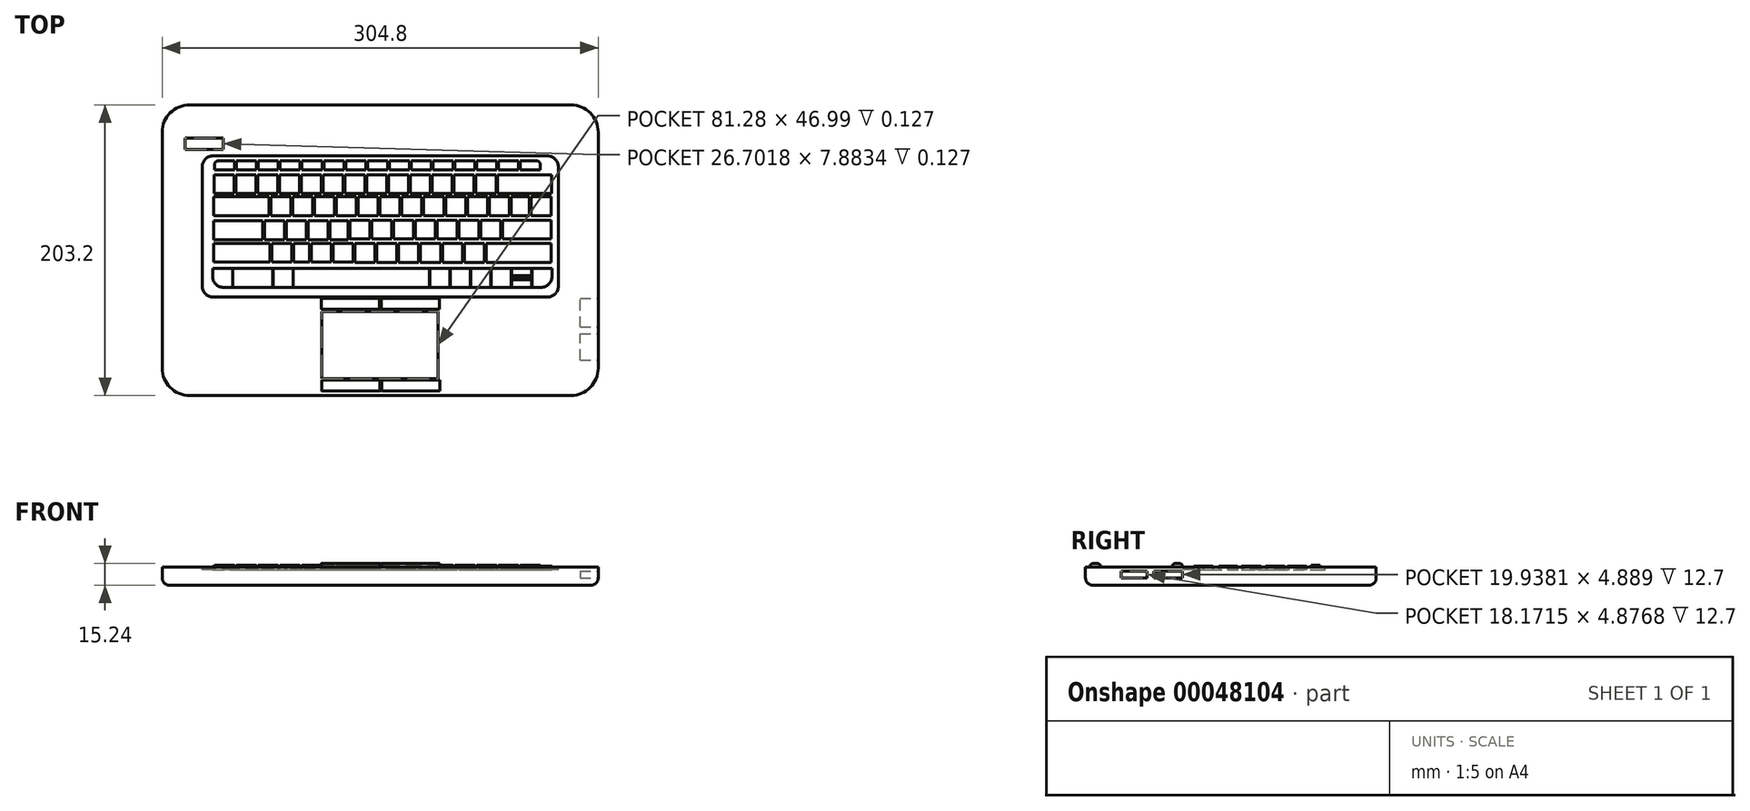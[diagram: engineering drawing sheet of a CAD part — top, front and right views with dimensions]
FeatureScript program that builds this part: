
annotation { "Feature Type Name" : "Feature", "Feature Type Description" : "" }
export const myFeature = defineFeature(function(context is Context, id is Id, definition is map)
    precondition{}
    {
        {
            var Q0;
            Q0=qCreatedBy(makeId("Top.planeOp"),FACE);
            var sketch = newSketch(context, id + "F0", { "sketchPlane" : qUnion([Q0])});
            skLineSegment(sketch, "E0.bottom", {"start": v(-133.35, 101.6) * mm, "end": v(133.35, 101.6) * mm});
            skLineSegment(sketch, "E0.top", {"start": v(-133.35, -101.6) * mm, "end": v(133.35, -101.6) * mm});
            skLineSegment(sketch, "E0.left", {"start": v(-152.4, 82.55) * mm, "end": v(-152.4, -82.55) * mm});
            skLineSegment(sketch, "E0.right", {"start": v(152.4, 82.55) * mm, "end": v(152.4, -82.55) * mm});
            skPoint(sketch, "E1.visualSharp", {"position": v(-152.4, 101.6) * mm});
            skArc(sketch, "E1.filletArc", {"start": v(-133.35, 101.6) * mm, "mid": v(-146.82, 96.02) * mm, "end": v(-152.4, 82.55) * mm});
            skPoint(sketch, "E2.visualSharp", {"position": v(152.4, 101.6) * mm});
            skArc(sketch, "E2.filletArc", {"start": v(152.4, 82.55) * mm, "mid": v(146.82, 96.02) * mm, "end": v(133.35, 101.6) * mm});
            skPoint(sketch, "E3.visualSharp", {"position": v(152.4, -101.6) * mm});
            skArc(sketch, "E3.filletArc", {"start": v(133.35, -101.6) * mm, "mid": v(146.82, -96.02) * mm, "end": v(152.4, -82.55) * mm});
            skPoint(sketch, "E4.visualSharp", {"position": v(-152.4, -101.6) * mm});
            skArc(sketch, "E4.filletArc", {"start": v(-152.4, -82.55) * mm, "mid": v(-146.82, -96.02) * mm, "end": v(-133.35, -101.6) * mm});
            skSolve(sketch);
        }
        {
            var Q0;
            Q0=makeQuery(id+"F0.imprint","IMPRINT",FACE,{"disambiguationData":[TD([[makeQuery(id+"F0.imprint","IMPRINT",EDGE,{"derivedFrom":sQuery(id+"F0.wireOp",EDGE,"E0.bottom")}),-1.0]])]});
            extrude(context, id + "F1", {"entities" : qUnion([Q0]), "depth" : 12.7 * mm});
        }
        {
            var Q0;
            Q0=makeQuery(id+"F1.opExtrude","CAP_EDGE",EDGE,{"disambiguationData":[OSD([sQuery(id+"F0.wireOp",EDGE,"E0.top")])],"isStart":true});
            fillet(context, id + "F2", {"entities" : qUnion([Q0]), "radius" : 5.08 * mm, "tangentPropagation" : true, "allowEdgeOverflow" : false});
        }
        {
            var Q0;
            Q0=makeQuery(id+"F1.opExtrude","CAP_FACE",FACE,{"disambiguationData":[OSD([sQuery(id+"F0.wireOp",EDGE,"E0.bottom"),sQuery(id+"F0.wireOp",EDGE,"E0.top"),sQuery(id+"F0.wireOp",EDGE,"E0.left"),sQuery(id+"F0.wireOp",EDGE,"E0.right"),sQuery(id+"F0.wireOp",EDGE,"E1.filletArc"),sQuery(id+"F0.wireOp",EDGE,"E2.filletArc"),sQuery(id+"F0.wireOp",EDGE,"E3.filletArc"),sQuery(id+"F0.wireOp",EDGE,"E4.filletArc")])],"isStart":false});
            var sketch = newSketch(context, id + "F3", { "sketchPlane" : qUnion([Q0])});
            skLineSegment(sketch, "E5.bottom", {"start": v(-116.84, -32.8) * mm, "end": v(116.84, -32.8) * mm});
            skLineSegment(sketch, "E5.top", {"start": v(-116.84, 65.93) * mm, "end": v(116.84, 65.93) * mm});
            skLineSegment(sketch, "E5.left", {"start": v(-124.46, -25.18) * mm, "end": v(-124.46, 58.31) * mm});
            skLineSegment(sketch, "E5.right", {"start": v(124.46, -25.18) * mm, "end": v(124.46, 58.31) * mm});
            skPoint(sketch, "E6.visualSharp", {"position": v(-124.46, 65.93) * mm});
            skArc(sketch, "E6.filletArc", {"start": v(-116.84, 65.93) * mm, "mid": v(-122.23, 63.7) * mm, "end": v(-124.46, 58.31) * mm});
            skPoint(sketch, "E7.visualSharp", {"position": v(124.46, 65.93) * mm});
            skArc(sketch, "E7.filletArc", {"start": v(124.46, 58.31) * mm, "mid": v(122.23, 63.7) * mm, "end": v(116.84, 65.93) * mm});
            skPoint(sketch, "E8.visualSharp", {"position": v(124.46, -32.8) * mm});
            skArc(sketch, "E8.filletArc", {"start": v(116.84, -32.8) * mm, "mid": v(122.23, -30.57) * mm, "end": v(124.46, -25.18) * mm});
            skPoint(sketch, "E9.visualSharp", {"position": v(-124.46, -32.8) * mm});
            skArc(sketch, "E9.filletArc", {"start": v(-124.46, -25.18) * mm, "mid": v(-122.23, -30.57) * mm, "end": v(-116.84, -32.8) * mm});
            skSolve(sketch);
        }
        {
            var Q0;
            Q0 = qSketchRegion(id + "F3", true);
            extrude(context, id + "F4", {"entities" : qUnion([Q0]), "operationType" : NewBodyOperationType.REMOVE, "oppositeDirection" : true, "depth" : 1.78 * mm});
        }
        {
            var Q0;
            Q0=makeQuery(id+"F4.boolean.opBoolean","COPY",FACE,{"derivedFrom":makeQuery(id+"F4.opExtrude","CAP_FACE",FACE,{"disambiguationData":[OSD([sQuery(id+"F3.wireOp",EDGE,"E5.bottom"),sQuery(id+"F3.wireOp",EDGE,"E5.top"),sQuery(id+"F3.wireOp",EDGE,"E5.left"),sQuery(id+"F3.wireOp",EDGE,"E5.right"),sQuery(id+"F3.wireOp",EDGE,"E6.filletArc"),sQuery(id+"F3.wireOp",EDGE,"E7.filletArc"),sQuery(id+"F3.wireOp",EDGE,"E8.filletArc"),sQuery(id+"F3.wireOp",EDGE,"E9.filletArc")])],"isStart":false})});
            var sketch = newSketch(context, id + "F5", { "sketchPlane" : qUnion([Q0])});
            skLineSegment(sketch, "E10.bottom", {"start": v(-60.72, -12.77) * mm, "end": v(34.53, -12.77) * mm});
            skLineSegment(sketch, "E10.top", {"start": v(-60.72, -25.99) * mm, "end": v(34.53, -25.99) * mm});
            skLineSegment(sketch, "E10.left", {"start": v(-60.72, -12.77) * mm, "end": v(-60.72, -25.99) * mm});
            skLineSegment(sketch, "E10.right", {"start": v(34.53, -12.77) * mm, "end": v(34.53, -25.99) * mm});
            skLineSegment(sketch, "E11.top", {"start": v(97.18, -32.93) * mm, "end": v(110.41, -32.93) * mm});
            skPoint(sketch, "E12.visualSharp", {"position": v(124.4, -32.93) * mm});
            skLineSegment(sketch, "E13.bottom", {"start": v(-60.97, -25.99) * mm, "end": v(-74.97, -25.99) * mm});
            skLineSegment(sketch, "E13.top", {"start": v(-60.97, -12.76) * mm, "end": v(-74.97, -12.76) * mm});
            skLineSegment(sketch, "E13.left", {"start": v(-60.97, -25.99) * mm, "end": v(-60.97, -12.76) * mm});
            skLineSegment(sketch, "E13.right", {"start": v(-74.97, -25.99) * mm, "end": v(-74.97, -12.76) * mm});
            skLineSegment(sketch, "E14.bottom", {"start": v(34.78, -12.76) * mm, "end": v(48.78, -12.76) * mm});
            skLineSegment(sketch, "E14.top", {"start": v(34.78, -25.99) * mm, "end": v(48.78, -25.99) * mm});
            skLineSegment(sketch, "E14.left", {"start": v(34.78, -12.76) * mm, "end": v(34.78, -25.99) * mm});
            skLineSegment(sketch, "E14.right", {"start": v(48.78, -12.76) * mm, "end": v(48.78, -25.99) * mm});
            skLineSegment(sketch, "E15.bottom", {"start": v(49.03, -12.76) * mm, "end": v(63.03, -12.76) * mm});
            skLineSegment(sketch, "E15.top", {"start": v(49.03, -25.99) * mm, "end": v(63.03, -25.99) * mm});
            skLineSegment(sketch, "E15.left", {"start": v(49.03, -12.76) * mm, "end": v(49.03, -25.99) * mm});
            skLineSegment(sketch, "E15.right", {"start": v(63.03, -12.76) * mm, "end": v(63.03, -25.99) * mm});
            skLineSegment(sketch, "E16.bottom", {"start": v(63.28, -12.76) * mm, "end": v(77.28, -12.76) * mm});
            skLineSegment(sketch, "E16.top", {"start": v(63.28, -25.99) * mm, "end": v(77.28, -25.99) * mm});
            skLineSegment(sketch, "E16.left", {"start": v(63.28, -12.76) * mm, "end": v(63.28, -25.99) * mm});
            skLineSegment(sketch, "E16.right", {"start": v(77.28, -12.76) * mm, "end": v(77.28, -25.99) * mm});
            skLineSegment(sketch, "E17", {"start": v(-88.97, -25.99) * mm, "end": v(-102.96, -25.99) * mm});
            skLineSegment(sketch, "E18", {"start": v(-102.96, -12.76) * mm, "end": v(-88.97, -12.76) * mm});
            skLineSegment(sketch, "E19.bottom", {"start": v(-117.21, -12.76) * mm, "end": v(-103.21, -12.76) * mm});
            skLineSegment(sketch, "E19.top", {"start": v(-109.6, -25.99) * mm, "end": v(-103.21, -25.99) * mm});
            skLineSegment(sketch, "E19.left", {"start": v(-117.21, -12.76) * mm, "end": v(-117.21, -18.37) * mm});
            skLineSegment(sketch, "E19.right", {"start": v(-103.21, -12.76) * mm, "end": v(-103.21, -25.99) * mm});
            skPoint(sketch, "E20.visualSharp", {"position": v(-117.21, -25.99) * mm});
            skArc(sketch, "E20.filletArc", {"start": v(-117.21, -18.37) * mm, "mid": v(-114.98, -23.76) * mm, "end": v(-109.6, -25.99) * mm});
            skLineSegment(sketch, "E21", {"start": v(-102.96, -12.76) * mm, "end": v(-102.96, -25.99) * mm});
            skLineSegment(sketch, "E22", {"start": v(-88.97, -12.76) * mm, "end": v(-102.96, -12.76) * mm});
            skLineSegment(sketch, "E23.bottom", {"start": v(77.53, -12.76) * mm, "end": v(91.53, -12.76) * mm});
            skLineSegment(sketch, "E23.top", {"start": v(77.53, -25.99) * mm, "end": v(91.53, -25.99) * mm});
            skLineSegment(sketch, "E23.left", {"start": v(77.53, -12.76) * mm, "end": v(77.53, -25.99) * mm});
            skLineSegment(sketch, "E23.right", {"start": v(91.53, -12.76) * mm, "end": v(91.53, -25.99) * mm});
            skPoint(sketch, "E24.visualSharp", {"position": v(129.05, -2.73) * mm});
            skLineSegment(sketch, "E25.top", {"start": v(91.78, -25.99) * mm, "end": v(105.78, -25.99) * mm});
            skLineSegment(sketch, "E25.left", {"start": v(91.78, -19.37) * mm, "end": v(91.78, -25.99) * mm});
            skLineSegment(sketch, "E25.right", {"start": v(105.78, -19.37) * mm, "end": v(105.78, -25.99) * mm});
            skLineSegment(sketch, "E26.top", {"start": v(248.95, -19.37) * mm, "end": v(262.95, -19.37) * mm});
            skLineSegment(sketch, "E27", {"start": v(-88.97, -12.76) * mm, "end": v(-88.97, -25.99) * mm});
            skLineSegment(sketch, "E28.bottom", {"start": v(-89.22, -12.76) * mm, "end": v(-75.22, -12.76) * mm});
            skLineSegment(sketch, "E28.top", {"start": v(-89.22, -25.99) * mm, "end": v(-75.22, -25.99) * mm});
            skLineSegment(sketch, "E28.left", {"start": v(-89.22, -12.76) * mm, "end": v(-89.22, -25.99) * mm});
            skLineSegment(sketch, "E28.right", {"start": v(-75.22, -12.76) * mm, "end": v(-75.22, -25.99) * mm});
            skLineSegment(sketch, "E29.bottom", {"start": v(106.03, -12.76) * mm, "end": v(120.03, -12.76) * mm});
            skLineSegment(sketch, "E29.top", {"start": v(106.03, -25.99) * mm, "end": v(112.4, -25.99) * mm});
            skLineSegment(sketch, "E29.left", {"start": v(106.03, -12.76) * mm, "end": v(106.03, -25.99) * mm});
            skLineSegment(sketch, "E29.right", {"start": v(120.03, -12.76) * mm, "end": v(120.03, -18.37) * mm});
            skArc(sketch, "E30.filletArc", {"start": v(112.4, -25.99) * mm, "mid": v(117.8, -23.76) * mm, "end": v(120.03, -18.37) * mm});
            skLineSegment(sketch, "E31.left", {"start": v(91.27, -12.5) * mm, "end": v(91.27, -19.12) * mm});
            skLineSegment(sketch, "E31.right", {"start": v(105.78, -12.5) * mm, "end": v(105.78, -19.12) * mm});
            skLineSegment(sketch, "E32", {"start": v(91.78, -19.37) * mm, "end": v(105.78, -19.37) * mm});
            skLineSegment(sketch, "E33.bottom", {"start": v(91.78, -12.63) * mm, "end": v(105.78, -12.63) * mm});
            skLineSegment(sketch, "E33.top", {"start": v(91.78, -19.25) * mm, "end": v(105.78, -19.25) * mm});
            skLineSegment(sketch, "E33.left", {"start": v(91.78, -12.63) * mm, "end": v(91.78, -19.25) * mm});
            skLineSegment(sketch, "E33.right", {"start": v(105.78, -12.63) * mm, "end": v(105.78, -19.25) * mm});
            skSolve(sketch);
        }
        {
            var Q0;
            Q0=makeQuery(id+"F5.imprint","IMPRINT",FACE,{"disambiguationData":[TD([[makeQuery(id+"F5.imprint","IMPRINT",EDGE,{"derivedFrom":sQuery(id+"F5.wireOp",EDGE,"E19.bottom")}),-1.0]])]});
            var Q1;
            Q1=makeQuery(id+"F5.imprint","IMPRINT",FACE,{"disambiguationData":[TD([[makeQuery(id+"F5.imprint","IMPRINT",EDGE,{"derivedFrom":sQuery(id+"F5.wireOp",EDGE,"E17")}),-1.0]])]});
            var Q2;
            {var subQ2=sQuery(id+"F5.wireOp",EDGE,"E27");Q2=makeQuery(id+"F5.imprint","IMPRINT",FACE,{"disambiguationData":[TD([[makeQuery(id+"F5.imprint","IMPRINT",EDGE,{"derivedFrom":subQ2}),1.0]])]});}
            var Q3;
            Q3=makeQuery(id+"F5.imprint","IMPRINT",FACE,{"disambiguationData":[TD([[makeQuery(id+"F5.imprint","IMPRINT",EDGE,{"derivedFrom":sQuery(id+"F5.wireOp",EDGE,"E13.bottom")}),-1.0]])]});
            var Q4;
            Q4=makeQuery(id+"F5.imprint","IMPRINT",FACE,{"disambiguationData":[TD([[makeQuery(id+"F5.imprint","IMPRINT",EDGE,{"derivedFrom":sQuery(id+"F5.wireOp",EDGE,"E10.bottom")}),-1.0]])]});
            var Q5;
            Q5=makeQuery(id+"F5.imprint","IMPRINT",FACE,{"disambiguationData":[TD([[makeQuery(id+"F5.imprint","IMPRINT",EDGE,{"derivedFrom":sQuery(id+"F5.wireOp",EDGE,"E14.bottom")}),-1.0]])]});
            var Q6;
            Q6=makeQuery(id+"F5.imprint","IMPRINT",FACE,{"disambiguationData":[TD([[makeQuery(id+"F5.imprint","IMPRINT",EDGE,{"derivedFrom":sQuery(id+"F5.wireOp",EDGE,"E15.bottom")}),-1.0]])]});
            var Q7;
            Q7=makeQuery(id+"F5.imprint","IMPRINT",FACE,{"disambiguationData":[TD([[makeQuery(id+"F5.imprint","IMPRINT",EDGE,{"derivedFrom":sQuery(id+"F5.wireOp",EDGE,"E16.bottom")}),-1.0]])]});
            var Q8;
            Q8=makeQuery(id+"F5.imprint","IMPRINT",FACE,{"disambiguationData":[TD([[makeQuery(id+"F5.imprint","IMPRINT",EDGE,{"derivedFrom":sQuery(id+"F5.wireOp",EDGE,"E23.top")}),1.0]])]});
            var Q9;
            Q9=makeQuery(id+"F5.imprint","IMPRINT",FACE,{"disambiguationData":[TD([[makeQuery(id+"F5.imprint","IMPRINT",EDGE,{"derivedFrom":sQuery(id+"F5.wireOp",EDGE,"E29.bottom")}),-1.0]])]});
            var Q10;
            {var subQ0=sQuery(id+"F5.wireOp",EDGE,"E33.bottom");Q10=makeQuery(id+"F5.imprint","IMPRINT",FACE,{"disambiguationData":[TD([[makeQuery(id+"F5.imprint","IMPRINT",EDGE,{"derivedFrom":subQ0}),-1.0]])]});}
            var Q11;
            Q11=makeQuery(id+"F5.imprint","IMPRINT",FACE,{"disambiguationData":[TD([[makeQuery(id+"F5.imprint","IMPRINT",EDGE,{"derivedFrom":sQuery(id+"F5.wireOp",EDGE,"E25.top")}),1.0]])]});
            extrude(context, id + "F6", {"entities" : qUnion([Q0, Q1, Q2, Q3, Q4, Q5, Q6, Q7, Q8, Q9, Q10, Q11]), "operationType" : NewBodyOperationType.ADD, "endBound" : BoundingType.SYMMETRIC, "depth" : 5.08 * mm});
        }
        {
            var Q0;
            Q0=makeQuery(id+"F6.opExtrude","CAP_EDGE",EDGE,{"disambiguationData":[OSD([sQuery(id+"F5.wireOp",EDGE,"E33.top")])],"isStart":false});
            chamfer(context, id + "F7", {"entities" : qUnion([Q0]), "width" : 1.27 * mm, "tangentPropagation" : true});
        }
        {
            var Q0;
            Q0=makeQuery(id+"F6.opExtrude","CAP_EDGE",EDGE,{"disambiguationData":[OSD([sQuery(id+"F5.wireOp",EDGE,"E32")])],"isStart":false});
            chamfer(context, id + "F8", {"entities" : qUnion([Q0]), "width" : 1.27 * mm, "tangentPropagation" : true});
        }
        {
            var Q0;
            Q0=makeQuery(id+"F4.boolean.opBoolean","COPY",FACE,{"derivedFrom":makeQuery(id+"F4.opExtrude","CAP_FACE",FACE,{"disambiguationData":[OSD([sQuery(id+"F3.wireOp",EDGE,"E5.bottom"),sQuery(id+"F3.wireOp",EDGE,"E5.top"),sQuery(id+"F3.wireOp",EDGE,"E5.left"),sQuery(id+"F3.wireOp",EDGE,"E5.right"),sQuery(id+"F3.wireOp",EDGE,"E6.filletArc"),sQuery(id+"F3.wireOp",EDGE,"E7.filletArc"),sQuery(id+"F3.wireOp",EDGE,"E8.filletArc"),sQuery(id+"F3.wireOp",EDGE,"E9.filletArc")])],"isStart":false})});
            var sketch = newSketch(context, id + "F9", { "sketchPlane" : qUnion([Q0])});
            skLineSegment(sketch, "E34.bottom", {"start": v(-76.47, 37.47) * mm, "end": v(-62.47, 37.47) * mm});
            skLineSegment(sketch, "E34.top", {"start": v(-76.47, 24.24) * mm, "end": v(-62.47, 24.24) * mm});
            skLineSegment(sketch, "E34.left", {"start": v(-76.47, 37.47) * mm, "end": v(-76.47, 24.24) * mm});
            skLineSegment(sketch, "E34.right", {"start": v(-62.47, 37.47) * mm, "end": v(-62.47, 24.24) * mm});
            skLineSegment(sketch, "E35.right", {"start": v(-47.2, 37.47) * mm, "end": v(-47.2, 24.24) * mm});
            skLineSegment(sketch, "E35.bottom", {"start": v(-61.2, 37.47) * mm, "end": v(-47.2, 37.47) * mm});
            skLineSegment(sketch, "E35.left", {"start": v(-61.2, 37.47) * mm, "end": v(-61.2, 24.24) * mm});
            skLineSegment(sketch, "E35.top", {"start": v(-61.2, 24.24) * mm, "end": v(-47.2, 24.24) * mm});
            skLineSegment(sketch, "E36.right", {"start": v(-31.94, 37.47) * mm, "end": v(-31.94, 24.24) * mm});
            skLineSegment(sketch, "E36.bottom", {"start": v(-45.94, 37.47) * mm, "end": v(-31.94, 37.47) * mm});
            skLineSegment(sketch, "E36.left", {"start": v(-45.94, 37.47) * mm, "end": v(-45.94, 24.24) * mm});
            skLineSegment(sketch, "E36.top", {"start": v(-45.94, 24.24) * mm, "end": v(-31.94, 24.24) * mm});
            skLineSegment(sketch, "E37.left", {"start": v(-30.67, 37.48) * mm, "end": v(-30.67, 24.25) * mm});
            skLineSegment(sketch, "E37.top", {"start": v(-30.67, 24.25) * mm, "end": v(-16.68, 24.25) * mm});
            skLineSegment(sketch, "E38.bottom", {"start": v(-34.44, 37.47) * mm, "end": v(-31.9, 37.47) * mm});
            skLineSegment(sketch, "E39.top", {"start": v(15.13, 24.24) * mm, "end": v(29.12, 24.24) * mm});
            skLineSegment(sketch, "E39.bottom", {"start": v(15.13, 37.47) * mm, "end": v(29.12, 37.47) * mm});
            skLineSegment(sketch, "E39.right", {"start": v(29.12, 37.47) * mm, "end": v(29.12, 24.24) * mm});
            skLineSegment(sketch, "E40.left", {"start": v(30.4, 37.47) * mm, "end": v(30.4, 24.24) * mm});
            skLineSegment(sketch, "E40.right", {"start": v(44.39, 37.47) * mm, "end": v(44.39, 24.24) * mm});
            skLineSegment(sketch, "E40.bottom", {"start": v(30.4, 37.47) * mm, "end": v(44.39, 37.47) * mm});
            skLineSegment(sketch, "E41.bottom", {"start": v(-0.14, 37.47) * mm, "end": v(13.86, 37.47) * mm});
            skLineSegment(sketch, "E42.right", {"start": v(-1.4, 37.47) * mm, "end": v(-1.4, 24.24) * mm});
            skLineSegment(sketch, "E41.top", {"start": v(-0.14, 24.24) * mm, "end": v(13.86, 24.24) * mm});
            skLineSegment(sketch, "E40.top", {"start": v(30.4, 24.24) * mm, "end": v(44.39, 24.24) * mm});
            skLineSegment(sketch, "E41.left", {"start": v(-0.14, 37.47) * mm, "end": v(-0.14, 24.24) * mm});
            skLineSegment(sketch, "E39.left", {"start": v(15.13, 37.47) * mm, "end": v(15.13, 24.24) * mm});
            skLineSegment(sketch, "E41.right", {"start": v(13.86, 37.47) * mm, "end": v(13.86, 24.24) * mm});
            skLineSegment(sketch, "E43.bottom", {"start": v(45.66, 37.47) * mm, "end": v(59.65, 37.47) * mm});
            skLineSegment(sketch, "E44.bottom", {"start": v(60.92, 37.47) * mm, "end": v(74.92, 37.47) * mm});
            skLineSegment(sketch, "E44.left", {"start": v(60.92, 37.47) * mm, "end": v(60.92, 24.24) * mm});
            skLineSegment(sketch, "E44.top", {"start": v(60.92, 24.24) * mm, "end": v(74.92, 24.24) * mm});
            skLineSegment(sketch, "E45.left", {"start": v(91.45, 37.47) * mm, "end": v(91.45, 24.24) * mm});
            skLineSegment(sketch, "E46.right", {"start": v(59.65, 37.47) * mm, "end": v(59.65, 24.24) * mm});
            skLineSegment(sketch, "E47.right", {"start": v(90.18, 37.47) * mm, "end": v(90.18, 24.24) * mm});
            skLineSegment(sketch, "E47.bottom", {"start": v(76.19, 37.47) * mm, "end": v(90.18, 37.47) * mm});
            skLineSegment(sketch, "E46.left", {"start": v(45.66, 37.47) * mm, "end": v(45.66, 24.24) * mm});
            skLineSegment(sketch, "E44.right", {"start": v(74.92, 37.47) * mm, "end": v(74.92, 24.24) * mm});
            skLineSegment(sketch, "E47.left", {"start": v(76.19, 37.47) * mm, "end": v(76.19, 24.24) * mm});
            skLineSegment(sketch, "E48.top", {"start": v(-48.16, -8.45) * mm, "end": v(-34.16, -8.45) * mm});
            skLineSegment(sketch, "E49.right", {"start": v(-61.9, 4.79) * mm, "end": v(-61.9, -8.45) * mm});
            skLineSegment(sketch, "E50.bottom", {"start": v(58.7, 4.7) * mm, "end": v(72.7, 4.7) * mm});
            skLineSegment(sketch, "E49.left", {"start": v(-75.89, 4.79) * mm, "end": v(-75.89, -8.45) * mm});
            skLineSegment(sketch, "E49.bottom", {"start": v(-75.89, 4.79) * mm, "end": v(-61.9, 4.79) * mm});
            skLineSegment(sketch, "E48.bottom", {"start": v(-48.16, 4.79) * mm, "end": v(-34.16, 4.79) * mm});
            skLineSegment(sketch, "E51.bottom", {"start": v(12.9, 4.7) * mm, "end": v(26.9, 4.7) * mm});
            skLineSegment(sketch, "E52.bottom", {"start": v(-2.36, 4.7) * mm, "end": v(11.64, 4.7) * mm});
            skLineSegment(sketch, "E53.left", {"start": v(-60.62, 4.79) * mm, "end": v(-60.62, -8.45) * mm});
            skLineSegment(sketch, "E54.top", {"start": v(43.44, -8.53) * mm, "end": v(57.43, -8.53) * mm});
            skLineSegment(sketch, "E48.right", {"start": v(-34.16, 4.79) * mm, "end": v(-34.16, -8.45) * mm});
            skLineSegment(sketch, "E54.left", {"start": v(43.44, 4.7) * mm, "end": v(43.44, -8.53) * mm});
            skLineSegment(sketch, "E55.right", {"start": v(-3.63, 4.7) * mm, "end": v(-3.63, -8.53) * mm});
            skLineSegment(sketch, "E56.right", {"start": v(42.17, 4.7) * mm, "end": v(42.17, -8.53) * mm});
            skLineSegment(sketch, "E54.bottom", {"start": v(43.44, 4.7) * mm, "end": v(57.43, 4.7) * mm});
            skLineSegment(sketch, "E51.top", {"start": v(12.9, -8.53) * mm, "end": v(26.9, -8.53) * mm});
            skLineSegment(sketch, "E49.top", {"start": v(-75.89, -8.45) * mm, "end": v(-61.9, -8.45) * mm});
            skLineSegment(sketch, "E56.bottom", {"start": v(28.17, 4.7) * mm, "end": v(42.17, 4.7) * mm});
            skLineSegment(sketch, "E57.left", {"start": v(-32.89, 4.79) * mm, "end": v(-32.89, -8.45) * mm});
            skLineSegment(sketch, "E56.top", {"start": v(28.17, -8.53) * mm, "end": v(42.17, -8.53) * mm});
            skLineSegment(sketch, "E53.bottom", {"start": v(-60.62, 4.79) * mm, "end": v(-49.43, 4.79) * mm});
            skLineSegment(sketch, "E52.top", {"start": v(-2.36, -8.53) * mm, "end": v(11.64, -8.53) * mm});
            skLineSegment(sketch, "E50.top", {"start": v(58.7, -8.53) * mm, "end": v(72.7, -8.53) * mm});
            skLineSegment(sketch, "E52.left", {"start": v(-2.36, 4.7) * mm, "end": v(-2.36, -8.53) * mm});
            skLineSegment(sketch, "E50.left", {"start": v(58.7, 4.7) * mm, "end": v(58.7, -8.53) * mm});
            skLineSegment(sketch, "E51.right", {"start": v(26.9, 4.7) * mm, "end": v(26.9, -8.53) * mm});
            skLineSegment(sketch, "E50.right", {"start": v(72.7, 4.7) * mm, "end": v(72.7, -8.53) * mm});
            skLineSegment(sketch, "E56.left", {"start": v(28.17, 4.7) * mm, "end": v(28.17, -8.53) * mm});
            skLineSegment(sketch, "E54.right", {"start": v(57.43, 4.7) * mm, "end": v(57.43, -8.53) * mm});
            skLineSegment(sketch, "E53.right", {"start": v(-49.43, 4.79) * mm, "end": v(-49.43, -8.45) * mm});
            skLineSegment(sketch, "E48.left", {"start": v(-48.16, 4.79) * mm, "end": v(-48.16, -8.45) * mm});
            skLineSegment(sketch, "E51.left", {"start": v(12.9, 4.7) * mm, "end": v(12.9, -8.53) * mm});
            skLineSegment(sketch, "E52.right", {"start": v(11.64, 4.7) * mm, "end": v(11.64, -8.53) * mm});
            skLineSegment(sketch, "E58.bottom", {"start": v(-149.52, 4.7) * mm, "end": v(-142.83, 4.7) * mm});
            skLineSegment(sketch, "E59.bottom", {"start": v(55.1, 20.98) * mm, "end": v(69.09, 20.98) * mm});
            skLineSegment(sketch, "E60.top", {"start": v(-50.28, 7.4) * mm, "end": v(-36.29, 7.4) * mm});
            skLineSegment(sketch, "E61.right", {"start": v(-66.82, 20.63) * mm, "end": v(-66.82, 7.4) * mm});
            skLineSegment(sketch, "E60.right", {"start": v(-36.29, 20.63) * mm, "end": v(-36.29, 7.4) * mm});
            skLineSegment(sketch, "E60.bottom", {"start": v(-50.28, 20.63) * mm, "end": v(-36.29, 20.63) * mm});
            skLineSegment(sketch, "E62.left", {"start": v(-65.55, 20.63) * mm, "end": v(-65.55, 7.4) * mm});
            skLineSegment(sketch, "E62.top", {"start": v(-65.55, 7.4) * mm, "end": v(-51.55, 7.4) * mm});
            skLineSegment(sketch, "E62.bottom", {"start": v(-65.55, 20.63) * mm, "end": v(-51.55, 20.63) * mm});
            skLineSegment(sketch, "E63.right", {"start": v(38.56, 20.98) * mm, "end": v(38.56, 7.75) * mm});
            skLineSegment(sketch, "E64.bottom", {"start": v(9.3, 20.98) * mm, "end": v(23.3, 20.98) * mm});
            skLineSegment(sketch, "E65.top", {"start": v(39.83, 7.75) * mm, "end": v(53.82, 7.75) * mm});
            skLineSegment(sketch, "E66.bottom", {"start": v(-5.97, 20.98) * mm, "end": v(8.02, 20.98) * mm});
            skLineSegment(sketch, "E67.bottom", {"start": v(70.36, 20.98) * mm, "end": v(84.35, 20.98) * mm});
            skLineSegment(sketch, "E68.right", {"start": v(-7.24, 20.98) * mm, "end": v(-7.24, 7.75) * mm});
            skLineSegment(sketch, "E65.left", {"start": v(39.83, 20.98) * mm, "end": v(39.83, 7.75) * mm});
            skLineSegment(sketch, "E67.right", {"start": v(84.35, 20.98) * mm, "end": v(84.35, 7.75) * mm});
            skLineSegment(sketch, "E63.top", {"start": v(24.56, 7.75) * mm, "end": v(38.56, 7.75) * mm});
            skLineSegment(sketch, "E67.top", {"start": v(70.36, 7.75) * mm, "end": v(84.35, 7.75) * mm});
            skLineSegment(sketch, "E59.left", {"start": v(55.1, 20.98) * mm, "end": v(55.1, 7.75) * mm});
            skLineSegment(sketch, "E64.right", {"start": v(23.3, 20.98) * mm, "end": v(23.3, 7.75) * mm});
            skLineSegment(sketch, "E66.top", {"start": v(-5.97, 7.75) * mm, "end": v(8.02, 7.75) * mm});
            skLineSegment(sketch, "E59.top", {"start": v(55.1, 7.75) * mm, "end": v(69.09, 7.75) * mm});
            skLineSegment(sketch, "E69.left", {"start": v(-35.02, 20.63) * mm, "end": v(-35.02, 7.4) * mm});
            skLineSegment(sketch, "E66.left", {"start": v(-5.97, 20.98) * mm, "end": v(-5.97, 7.75) * mm});
            skLineSegment(sketch, "E63.left", {"start": v(24.56, 20.98) * mm, "end": v(24.56, 7.75) * mm});
            skLineSegment(sketch, "E65.right", {"start": v(53.82, 20.98) * mm, "end": v(53.82, 7.75) * mm});
            skLineSegment(sketch, "E61.bottom", {"start": v(-80.81, 20.63) * mm, "end": v(-66.82, 20.63) * mm});
            skLineSegment(sketch, "E61.top", {"start": v(-80.81, 7.4) * mm, "end": v(-66.82, 7.4) * mm});
            skLineSegment(sketch, "E65.bottom", {"start": v(39.83, 20.98) * mm, "end": v(53.82, 20.98) * mm});
            skLineSegment(sketch, "E64.top", {"start": v(9.3, 7.75) * mm, "end": v(23.3, 7.75) * mm});
            skLineSegment(sketch, "E62.right", {"start": v(-51.55, 20.63) * mm, "end": v(-51.55, 7.4) * mm});
            skLineSegment(sketch, "E60.left", {"start": v(-50.28, 20.63) * mm, "end": v(-50.28, 7.4) * mm});
            skLineSegment(sketch, "E64.left", {"start": v(9.3, 20.98) * mm, "end": v(9.3, 7.75) * mm});
            skLineSegment(sketch, "E66.right", {"start": v(8.02, 20.98) * mm, "end": v(8.02, 7.75) * mm});
            skLineSegment(sketch, "E59.right", {"start": v(69.09, 20.98) * mm, "end": v(69.09, 7.75) * mm});
            skLineSegment(sketch, "E67.left", {"start": v(70.36, 20.98) * mm, "end": v(70.36, 7.75) * mm});
            skLineSegment(sketch, "E70.bottom", {"start": v(-33.12, 20.63) * mm, "end": v(-30.58, 20.63) * mm});
            skLineSegment(sketch, "E71.bottom", {"start": v(11.65, 20.63) * mm, "end": v(14.2, 20.63) * mm});
            skLineSegment(sketch, "E72.bottom", {"start": v(-85.72, 52.78) * mm, "end": v(-71.72, 52.78) * mm});
            skLineSegment(sketch, "E72.top", {"start": v(-85.72, 39.55) * mm, "end": v(-71.72, 39.55) * mm});
            skLineSegment(sketch, "E73.bottom", {"start": v(5.87, 52.78) * mm, "end": v(19.87, 52.78) * mm});
            skLineSegment(sketch, "E74.top", {"start": v(-24.66, 39.55) * mm, "end": v(-10.66, 39.55) * mm});
            skLineSegment(sketch, "E75.right", {"start": v(-41.2, 52.78) * mm, "end": v(-41.2, 39.55) * mm});
            skLineSegment(sketch, "E73.left", {"start": v(5.87, 52.78) * mm, "end": v(5.87, 39.55) * mm});
            skLineSegment(sketch, "E76.bottom", {"start": v(-116.25, 52.78) * mm, "end": v(-102.26, 52.78) * mm});
            skLineSegment(sketch, "E76.left", {"start": v(-116.25, 52.78) * mm, "end": v(-116.25, 39.55) * mm});
            skLineSegment(sketch, "E76.top", {"start": v(-116.25, 39.55) * mm, "end": v(-102.26, 39.55) * mm});
            skLineSegment(sketch, "E77.bottom", {"start": v(21.14, 52.78) * mm, "end": v(35.13, 52.78) * mm});
            skLineSegment(sketch, "E76.right", {"start": v(-102.26, 52.78) * mm, "end": v(-102.26, 39.55) * mm});
            skLineSegment(sketch, "E78.top", {"start": v(66.9, 39.55) * mm, "end": v(80.9, 39.55) * mm});
            skLineSegment(sketch, "E78.bottom", {"start": v(66.9, 52.78) * mm, "end": v(80.9, 52.78) * mm});
            skLineSegment(sketch, "E79.top", {"start": v(-70.45, 39.55) * mm, "end": v(-56.46, 39.55) * mm});
            skLineSegment(sketch, "E80.bottom", {"start": v(-9.4, 52.78) * mm, "end": v(4.6, 52.78) * mm});
            skLineSegment(sketch, "E81.top", {"start": v(-100.99, 39.55) * mm, "end": v(-87, 39.55) * mm});
            skLineSegment(sketch, "E81.left", {"start": v(-100.99, 52.78) * mm, "end": v(-100.99, 39.55) * mm});
            skLineSegment(sketch, "E74.bottom", {"start": v(-24.66, 52.78) * mm, "end": v(-10.66, 52.78) * mm});
            skLineSegment(sketch, "E81.bottom", {"start": v(-100.99, 52.78) * mm, "end": v(-87, 52.78) * mm});
            skLineSegment(sketch, "E82.bottom", {"start": v(-39.92, 52.78) * mm, "end": v(-25.93, 52.78) * mm});
            skLineSegment(sketch, "E82.top", {"start": v(-39.92, 39.55) * mm, "end": v(-25.93, 39.55) * mm});
            skLineSegment(sketch, "E77.top", {"start": v(21.14, 39.55) * mm, "end": v(35.13, 39.55) * mm});
            skLineSegment(sketch, "E73.right", {"start": v(19.87, 52.78) * mm, "end": v(19.87, 39.55) * mm});
            skLineSegment(sketch, "E83.top", {"start": v(36.4, 39.55) * mm, "end": v(50.4, 39.55) * mm});
            skLineSegment(sketch, "E77.left", {"start": v(21.14, 52.78) * mm, "end": v(21.14, 39.55) * mm});
            skLineSegment(sketch, "E80.top", {"start": v(-9.4, 39.55) * mm, "end": v(4.6, 39.55) * mm});
            skLineSegment(sketch, "E78.right", {"start": v(80.9, 52.78) * mm, "end": v(80.9, 39.55) * mm});
            skLineSegment(sketch, "E82.left", {"start": v(-39.92, 52.78) * mm, "end": v(-39.92, 39.55) * mm});
            skLineSegment(sketch, "E83.left", {"start": v(36.4, 52.78) * mm, "end": v(36.4, 39.55) * mm});
            skLineSegment(sketch, "E72.left", {"start": v(-85.72, 52.78) * mm, "end": v(-85.72, 39.55) * mm});
            skLineSegment(sketch, "E81.right", {"start": v(-87, 52.78) * mm, "end": v(-87, 39.55) * mm});
            skLineSegment(sketch, "E72.right", {"start": v(-71.72, 52.78) * mm, "end": v(-71.72, 39.55) * mm});
            skLineSegment(sketch, "E84.bottom", {"start": v(-6.45, 52.78) * mm, "end": v(-3.9, 52.78) * mm});
            skLineSegment(sketch, "E74.right", {"start": v(-10.66, 52.78) * mm, "end": v(-10.66, 39.55) * mm});
            skLineSegment(sketch, "E80.left", {"start": v(-9.4, 52.78) * mm, "end": v(-9.4, 39.55) * mm});
            skLineSegment(sketch, "E85.left", {"start": v(51.67, 52.78) * mm, "end": v(51.67, 39.55) * mm});
            skLineSegment(sketch, "E74.left", {"start": v(-24.66, 52.78) * mm, "end": v(-24.66, 39.55) * mm});
            skLineSegment(sketch, "E82.right", {"start": v(-25.93, 52.78) * mm, "end": v(-25.93, 39.55) * mm});
            skLineSegment(sketch, "E86.bottom", {"start": v(-51.22, 52.78) * mm, "end": v(-48.68, 52.78) * mm});
            skLineSegment(sketch, "E77.right", {"start": v(35.13, 52.78) * mm, "end": v(35.13, 39.55) * mm});
            skLineSegment(sketch, "E79.left", {"start": v(-70.45, 52.78) * mm, "end": v(-70.45, 39.55) * mm});
            skLineSegment(sketch, "E83.right", {"start": v(50.4, 52.78) * mm, "end": v(50.4, 39.55) * mm});
            skLineSegment(sketch, "E87", {"start": v(45.66, 24.24) * mm, "end": v(59.65, 24.24) * mm});
            skLineSegment(sketch, "E88", {"start": v(76.19, 24.24) * mm, "end": v(90.18, 24.24) * mm});
            skLineSegment(sketch, "E89.left", {"start": v(-116.5, 4.79) * mm, "end": v(-116.5, -8.45) * mm});
            skLineSegment(sketch, "E90", {"start": v(-116.5, 4.79) * mm, "end": v(-77.16, 4.79) * mm});
            skLineSegment(sketch, "E91", {"start": v(-77.16, 4.79) * mm, "end": v(-77.16, -8.45) * mm});
            skLineSegment(sketch, "E92", {"start": v(-77.16, -8.45) * mm, "end": v(-116.5, -8.45) * mm});
            skLineSegment(sketch, "E93.bottom", {"start": v(73.97, 4.7) * mm, "end": v(119.33, 4.7) * mm});
            skLineSegment(sketch, "E93.top", {"start": v(73.97, -8.53) * mm, "end": v(119.33, -8.53) * mm});
            skLineSegment(sketch, "E93.left", {"start": v(73.97, 4.7) * mm, "end": v(73.97, -8.53) * mm});
            skLineSegment(sketch, "E93.right", {"start": v(119.33, 4.7) * mm, "end": v(119.33, -8.53) * mm});
            skLineSegment(sketch, "E94", {"start": v(-80.81, 7.4) * mm, "end": v(-80.81, 20.63) * mm});
            skLineSegment(sketch, "E95.bottom", {"start": v(-116.32, 20.63) * mm, "end": v(-82.08, 20.63) * mm});
            skLineSegment(sketch, "E95.top", {"start": v(-116.32, 7.4) * mm, "end": v(-82.08, 7.4) * mm});
            skLineSegment(sketch, "E95.left", {"start": v(-116.32, 20.63) * mm, "end": v(-116.32, 7.4) * mm});
            skLineSegment(sketch, "E95.right", {"start": v(-82.08, 20.63) * mm, "end": v(-82.08, 7.4) * mm});
            skLineSegment(sketch, "E96.bottom", {"start": v(85.62, 20.98) * mm, "end": v(119.4, 20.98) * mm});
            skLineSegment(sketch, "E96.top", {"start": v(85.62, 7.75) * mm, "end": v(119.4, 7.75) * mm});
            skLineSegment(sketch, "E96.left", {"start": v(85.62, 20.98) * mm, "end": v(85.62, 7.75) * mm});
            skLineSegment(sketch, "E96.right", {"start": v(119.4, 20.98) * mm, "end": v(119.4, 7.75) * mm});
            skLineSegment(sketch, "E97.bottom", {"start": v(-116.32, 37.47) * mm, "end": v(-77.74, 37.47) * mm});
            skLineSegment(sketch, "E97.top", {"start": v(-116.32, 24.24) * mm, "end": v(-77.74, 24.24) * mm});
            skLineSegment(sketch, "E97.left", {"start": v(-116.32, 37.47) * mm, "end": v(-116.32, 24.24) * mm});
            skLineSegment(sketch, "E97.right", {"start": v(-77.74, 37.47) * mm, "end": v(-77.74, 24.24) * mm});
            skLineSegment(sketch, "E98.bottom", {"start": v(82.17, 52.78) * mm, "end": v(119.73, 52.78) * mm});
            skLineSegment(sketch, "E98.top", {"start": v(82.17, 39.67) * mm, "end": v(119.73, 39.67) * mm});
            skLineSegment(sketch, "E98.left", {"start": v(82.17, 52.78) * mm, "end": v(82.17, 39.67) * mm});
            skLineSegment(sketch, "E98.right", {"start": v(119.73, 52.78) * mm, "end": v(119.73, 39.67) * mm});
            skLineSegment(sketch, "E99", {"start": v(-70.45, 52.78) * mm, "end": v(-56.46, 52.78) * mm});
            skLineSegment(sketch, "E100", {"start": v(-56.46, 52.78) * mm, "end": v(-56.46, 39.55) * mm});
            skLineSegment(sketch, "E101", {"start": v(-41.2, 52.78) * mm, "end": v(-55.19, 52.78) * mm});
            skLineSegment(sketch, "E102", {"start": v(-55.19, 52.78) * mm, "end": v(-55.19, 39.63) * mm});
            skLineSegment(sketch, "E103", {"start": v(-55.19, 39.63) * mm, "end": v(-41.2, 39.55) * mm});
            skLineSegment(sketch, "E104", {"start": v(50.4, 52.78) * mm, "end": v(36.4, 52.78) * mm});
            skLineSegment(sketch, "E105", {"start": v(5.87, 39.55) * mm, "end": v(19.87, 39.55) * mm});
            skLineSegment(sketch, "E106", {"start": v(66.9, 39.55) * mm, "end": v(66.9, 52.78) * mm});
            skLineSegment(sketch, "E107", {"start": v(51.67, 39.55) * mm, "end": v(65.64, 39.55) * mm});
            skLineSegment(sketch, "E108", {"start": v(65.64, 39.55) * mm, "end": v(65.64, 52.78) * mm});
            skLineSegment(sketch, "E109", {"start": v(65.64, 52.78) * mm, "end": v(51.67, 52.78) * mm});
            skLineSegment(sketch, "E110", {"start": v(4.6, 52.78) * mm, "end": v(4.6, 39.55) * mm});
            skLineSegment(sketch, "E111", {"start": v(-16.68, 24.25) * mm, "end": v(-16.68, 37.42) * mm});
            skLineSegment(sketch, "E112", {"start": v(-16.68, 37.42) * mm, "end": v(-30.67, 37.48) * mm});
            skLineSegment(sketch, "E113", {"start": v(-1.4, 37.47) * mm, "end": v(-15.4, 37.47) * mm});
            skLineSegment(sketch, "E114", {"start": v(-15.4, 37.47) * mm, "end": v(-15.4, 24.24) * mm});
            skLineSegment(sketch, "E115", {"start": v(-15.4, 24.24) * mm, "end": v(-1.4, 24.24) * mm});
            skLineSegment(sketch, "E116", {"start": v(91.45, 37.47) * mm, "end": v(104.18, 37.47) * mm});
            skLineSegment(sketch, "E117", {"start": v(119.45, 24.24) * mm, "end": v(119.45, 37.47) * mm});
            skLineSegment(sketch, "E118", {"start": v(119.45, 37.47) * mm, "end": v(105.45, 37.47) * mm});
            skLineSegment(sketch, "E119", {"start": v(104.18, 37.47) * mm, "end": v(104.18, 24.24) * mm});
            skLineSegment(sketch, "E120", {"start": v(104.18, 24.24) * mm, "end": v(91.45, 24.24) * mm});
            skLineSegment(sketch, "E121", {"start": v(105.45, 37.47) * mm, "end": v(105.45, 24.24) * mm});
            skLineSegment(sketch, "E122", {"start": v(105.45, 24.24) * mm, "end": v(119.45, 24.24) * mm});
            skLineSegment(sketch, "E123", {"start": v(-35.02, 7.4) * mm, "end": v(-22.5, 7.4) * mm});
            skLineSegment(sketch, "E124", {"start": v(-22.5, 7.4) * mm, "end": v(-22.5, 20.63) * mm});
            skLineSegment(sketch, "E125", {"start": v(-22.5, 20.63) * mm, "end": v(-35.02, 20.63) * mm});
            skLineSegment(sketch, "E126", {"start": v(-7.24, 20.98) * mm, "end": v(-21.24, 20.98) * mm});
            skLineSegment(sketch, "E127", {"start": v(-21.24, 20.98) * mm, "end": v(-21.24, 7.75) * mm});
            skLineSegment(sketch, "E128", {"start": v(-21.24, 7.75) * mm, "end": v(-7.24, 7.75) * mm});
            skLineSegment(sketch, "E129", {"start": v(-3.63, 4.7) * mm, "end": v(-17.62, 4.7) * mm});
            skLineSegment(sketch, "E130", {"start": v(-17.62, 4.7) * mm, "end": v(-3.63, 4.7) * mm});
            skLineSegment(sketch, "E131", {"start": v(-3.63, -8.53) * mm, "end": v(-17.62, -8.53) * mm});
            skLineSegment(sketch, "E132", {"start": v(-17.62, -8.53) * mm, "end": v(-17.62, 4.7) * mm});
            skLineSegment(sketch, "E133", {"start": v(-32.89, 4.79) * mm, "end": v(-16.51, 4.79) * mm});
            skLineSegment(sketch, "E134", {"start": v(-18.9, 4.79) * mm, "end": v(-18.9, -8.45) * mm});
            skLineSegment(sketch, "E135", {"start": v(-18.9, -8.45) * mm, "end": v(-32.89, -8.45) * mm});
            skLineSegment(sketch, "E136", {"start": v(-60.62, -8.45) * mm, "end": v(-49.43, -8.45) * mm});
            skLineSegment(sketch, "E137", {"start": v(24.56, 20.98) * mm, "end": v(38.56, 20.98) * mm});
            skSolve(sketch);
        }
        {
            var Q0;
            Q0 = qSketchRegion(id + "F9", true);
            extrude(context, id + "F10", {"entities" : qUnion([Q0]), "operationType" : NewBodyOperationType.ADD, "depth" : 2.54 * mm});
        }
        {
            var Q0;
            Q0=makeQuery(id+"F3.imprint","IMPRINT",FACE,{"disambiguationData":[TD([[makeQuery(id+"F3.imprint","IMPRINT",EDGE,{"derivedFrom":sQuery(id+"F3.wireOp",EDGE,"E5.bottom")}),-1.0]])]});
            var sketch = newSketch(context, id + "F11", { "sketchPlane" : qUnion([Q0])});
            skLineSegment(sketch, "E138.bottom", {"start": v(41.48, -41.19) * mm, "end": v(0.84, -41.19) * mm});
            skLineSegment(sketch, "E138.top", {"start": v(41.48, -33.57) * mm, "end": v(0.84, -33.57) * mm});
            skLineSegment(sketch, "E138.left", {"start": v(41.48, -41.19) * mm, "end": v(41.48, -33.57) * mm});
            skLineSegment(sketch, "E138.right", {"start": v(0.84, -41.19) * mm, "end": v(0.84, -33.57) * mm});
            skLineSegment(sketch, "E139.bottom", {"start": v(-41.07, -33.57) * mm, "end": v(-0.43, -33.57) * mm});
            skLineSegment(sketch, "E139.top", {"start": v(-41.07, -41.19) * mm, "end": v(-0.43, -41.19) * mm});
            skLineSegment(sketch, "E139.left", {"start": v(-41.07, -33.57) * mm, "end": v(-41.07, -41.19) * mm});
            skLineSegment(sketch, "E139.right", {"start": v(-0.43, -33.57) * mm, "end": v(-0.43, -41.19) * mm});
            skLineSegment(sketch, "E140.top", {"start": v(41.82, -90.97) * mm, "end": v(1.18, -90.97) * mm});
            skLineSegment(sketch, "E141.bottom", {"start": v(-40.73, -90.97) * mm, "end": v(-0.09, -90.97) * mm});
            skLineSegment(sketch, "E140.left", {"start": v(41.82, -98.59) * mm, "end": v(41.82, -90.97) * mm});
            skLineSegment(sketch, "E141.right", {"start": v(-0.09, -90.97) * mm, "end": v(-0.09, -98.59) * mm});
            skLineSegment(sketch, "E140.bottom", {"start": v(41.82, -98.59) * mm, "end": v(1.18, -98.59) * mm});
            skLineSegment(sketch, "E140.right", {"start": v(1.18, -98.59) * mm, "end": v(1.18, -90.97) * mm});
            skLineSegment(sketch, "E141.top", {"start": v(-40.73, -98.59) * mm, "end": v(-0.09, -98.59) * mm});
            skLineSegment(sketch, "E141.left", {"start": v(-40.73, -90.97) * mm, "end": v(-40.73, -98.59) * mm});
            skSolve(sketch);
        }
        {
            var Q0;
            Q0 = qSketchRegion(id + "F11", true);
            extrude(context, id + "F12", {"entities" : qUnion([Q0]), "operationType" : NewBodyOperationType.ADD, "depth" : 2.54 * mm});
        }
        {
            var Q0;
            Q0=makeQuery(id+"F12.opExtrude","CAP_EDGE",EDGE,{"disambiguationData":[OSD([sQuery(id+"F11.wireOp",EDGE,"E138.bottom")])],"isStart":false});
            var Q1;
            Q1=makeQuery(id+"F12.opExtrude","CAP_EDGE",EDGE,{"disambiguationData":[OSD([sQuery(id+"F11.wireOp",EDGE,"E138.top")])],"isStart":false});
            fillet(context, id + "F13", {"entities" : qUnion([Q0, Q1]), "radius" : 2.54 * mm, "tangentPropagation" : true, "allowEdgeOverflow" : false});
        }
        {
            var Q0;
            Q0=makeQuery(id+"F12.opExtrude","CAP_EDGE",EDGE,{"disambiguationData":[OSD([sQuery(id+"F11.wireOp",EDGE,"E139.top")])],"isStart":false});
            var Q1;
            Q1=makeQuery(id+"F12.opExtrude","CAP_EDGE",EDGE,{"disambiguationData":[OSD([sQuery(id+"F11.wireOp",EDGE,"E139.bottom")])],"isStart":false});
            var Q2;
            Q2=makeQuery(id+"F12.opExtrude","CAP_EDGE",EDGE,{"disambiguationData":[OSD([sQuery(id+"F11.wireOp",EDGE,"E141.bottom")])],"isStart":false});
            var Q3;
            Q3=makeQuery(id+"F12.opExtrude","CAP_EDGE",EDGE,{"disambiguationData":[OSD([sQuery(id+"F11.wireOp",EDGE,"E140.top")])],"isStart":false});
            fillet(context, id + "F14", {"entities" : qUnion([Q0, Q1, Q2, Q3]), "radius" : 2.54 * mm, "tangentPropagation" : true, "allowEdgeOverflow" : false});
        }
        {
            var Q0;
            Q0=makeQuery(id+"F12.opExtrude","CAP_EDGE",EDGE,{"disambiguationData":[OSD([sQuery(id+"F11.wireOp",EDGE,"E141.top")])],"isStart":false});
            var Q1;
            Q1=makeQuery(id+"F12.opExtrude","CAP_EDGE",EDGE,{"disambiguationData":[OSD([sQuery(id+"F11.wireOp",EDGE,"E140.bottom")])],"isStart":false});
            fillet(context, id + "F15", {"entities" : qUnion([Q0, Q1]), "radius" : 2.54 * mm, "tangentPropagation" : true, "allowEdgeOverflow" : false});
        }
        {
            var Q0;
            Q0=makeQuery(id+"F3.imprint","IMPRINT",FACE,{"disambiguationData":[TD([[makeQuery(id+"F3.imprint","IMPRINT",EDGE,{"derivedFrom":sQuery(id+"F3.wireOp",EDGE,"E5.bottom")}),-1.0]])]});
            var sketch = newSketch(context, id + "F16", { "sketchPlane" : qUnion([Q0])});
            skLineSegment(sketch, "E142.bottom", {"start": v(-40.8, -43.03) * mm, "end": v(40.47, -43.03) * mm});
            skLineSegment(sketch, "E142.top", {"start": v(-40.8, -90.02) * mm, "end": v(40.47, -90.02) * mm});
            skLineSegment(sketch, "E142.left", {"start": v(-40.8, -43.03) * mm, "end": v(-40.8, -90.02) * mm});
            skLineSegment(sketch, "E142.right", {"start": v(40.47, -43.03) * mm, "end": v(40.47, -90.02) * mm});
            skSolve(sketch);
        }
        {
            var Q0;
            Q0 = qSketchRegion(id + "F16", true);
            extrude(context, id + "F17", {"entities" : qUnion([Q0]), "operationType" : NewBodyOperationType.REMOVE, "oppositeDirection" : true, "depth" : 0.13 * mm});
        }
        {
            var Q0;
            Q0=makeQuery(id+"F3.imprint","IMPRINT",FACE,{"disambiguationData":[TD([[makeQuery(id+"F3.imprint","IMPRINT",EDGE,{"derivedFrom":sQuery(id+"F3.wireOp",EDGE,"E5.bottom")}),1.0]])]});
            var sketch = newSketch(context, id + "F18", { "sketchPlane" : qUnion([Q0])});
            skLineSegment(sketch, "E143.bottom", {"start": v(-113.21, 62.4) * mm, "end": v(-101.76, 62.4) * mm});
            skLineSegment(sketch, "E143.top", {"start": v(-115.75, 56.01) * mm, "end": v(-101.76, 56.01) * mm});
            skLineSegment(sketch, "E143.left", {"start": v(-115.75, 59.86) * mm, "end": v(-115.75, 56.01) * mm});
            skLineSegment(sketch, "E143.right", {"start": v(-101.76, 62.4) * mm, "end": v(-101.76, 56.01) * mm});
            skPoint(sketch, "E144.visualSharp", {"position": v(-115.75, 62.4) * mm});
            skArc(sketch, "E144.filletArc", {"start": v(-113.21, 62.4) * mm, "mid": v(-115, 61.65) * mm, "end": v(-115.75, 59.86) * mm});
            skLineSegment(sketch, "E145.bottom", {"start": v(-100.49, 62.4) * mm, "end": v(-86.5, 62.4) * mm});
            skLineSegment(sketch, "E145.top", {"start": v(-100.49, 56.02) * mm, "end": v(-86.5, 56.02) * mm});
            skLineSegment(sketch, "E145.left", {"start": v(-100.49, 62.4) * mm, "end": v(-100.49, 56.02) * mm});
            skLineSegment(sketch, "E145.right", {"start": v(-86.5, 62.4) * mm, "end": v(-86.5, 56.02) * mm});
            skLineSegment(sketch, "E146.bottom", {"start": v(-85.22, 62.4) * mm, "end": v(-71.23, 62.4) * mm});
            skLineSegment(sketch, "E146.top", {"start": v(-85.22, 56.02) * mm, "end": v(-71.23, 56.02) * mm});
            skLineSegment(sketch, "E146.left", {"start": v(-85.22, 62.4) * mm, "end": v(-85.22, 56.02) * mm});
            skLineSegment(sketch, "E146.right", {"start": v(-71.23, 62.4) * mm, "end": v(-71.23, 56.02) * mm});
            skLineSegment(sketch, "E147.bottom", {"start": v(-54.7, 62.4) * mm, "end": v(-40.7, 62.4) * mm});
            skLineSegment(sketch, "E148.left", {"start": v(-69.96, 62.4) * mm, "end": v(-69.96, 56.02) * mm});
            skLineSegment(sketch, "E148.right", {"start": v(-55.96, 62.4) * mm, "end": v(-55.96, 56.02) * mm});
            skLineSegment(sketch, "E147.right", {"start": v(-40.7, 62.4) * mm, "end": v(-40.7, 56.02) * mm});
            skLineSegment(sketch, "E147.left", {"start": v(-54.7, 62.4) * mm, "end": v(-54.7, 56.02) * mm});
            skLineSegment(sketch, "E148.bottom", {"start": v(-69.96, 62.4) * mm, "end": v(-55.96, 62.4) * mm});
            skLineSegment(sketch, "E148.top", {"start": v(-69.96, 56.02) * mm, "end": v(-55.96, 56.02) * mm});
            skLineSegment(sketch, "E147.top", {"start": v(-54.7, 56.02) * mm, "end": v(-40.7, 56.02) * mm});
            skLineSegment(sketch, "E149.bottom", {"start": v(-24.16, 62.4) * mm, "end": v(-10.16, 62.4) * mm});
            skLineSegment(sketch, "E150.left", {"start": v(-39.42, 62.4) * mm, "end": v(-39.42, 56.02) * mm});
            skLineSegment(sketch, "E150.right", {"start": v(-25.43, 62.4) * mm, "end": v(-25.43, 56.02) * mm});
            skLineSegment(sketch, "E149.right", {"start": v(-10.16, 62.4) * mm, "end": v(-10.16, 56.02) * mm});
            skLineSegment(sketch, "E149.left", {"start": v(-24.16, 62.4) * mm, "end": v(-24.16, 56.02) * mm});
            skLineSegment(sketch, "E150.bottom", {"start": v(-39.42, 62.4) * mm, "end": v(-25.43, 62.4) * mm});
            skLineSegment(sketch, "E150.top", {"start": v(-39.42, 56.02) * mm, "end": v(-25.43, 56.02) * mm});
            skLineSegment(sketch, "E149.top", {"start": v(-24.16, 56.02) * mm, "end": v(-10.16, 56.02) * mm});
            skLineSegment(sketch, "E151.bottom", {"start": v(6.37, 62.4) * mm, "end": v(20.37, 62.4) * mm});
            skLineSegment(sketch, "E152.left", {"start": v(-8.9, 62.4) * mm, "end": v(-8.9, 56.02) * mm});
            skLineSegment(sketch, "E152.right", {"start": v(5.1, 62.4) * mm, "end": v(5.1, 56.02) * mm});
            skLineSegment(sketch, "E151.right", {"start": v(20.37, 62.4) * mm, "end": v(20.37, 56.02) * mm});
            skLineSegment(sketch, "E151.left", {"start": v(6.37, 62.4) * mm, "end": v(6.37, 56.02) * mm});
            skLineSegment(sketch, "E152.bottom", {"start": v(-8.9, 62.4) * mm, "end": v(5.1, 62.4) * mm});
            skLineSegment(sketch, "E152.top", {"start": v(-8.9, 56.02) * mm, "end": v(5.1, 56.02) * mm});
            skLineSegment(sketch, "E151.top", {"start": v(6.37, 56.02) * mm, "end": v(20.37, 56.02) * mm});
            skLineSegment(sketch, "E153.bottom", {"start": v(36.9, 62.4) * mm, "end": v(50.9, 62.4) * mm});
            skLineSegment(sketch, "E154.left", {"start": v(21.64, 62.4) * mm, "end": v(21.64, 56.02) * mm});
            skLineSegment(sketch, "E154.right", {"start": v(35.63, 62.4) * mm, "end": v(35.63, 56.02) * mm});
            skLineSegment(sketch, "E153.right", {"start": v(50.9, 62.4) * mm, "end": v(50.9, 56.02) * mm});
            skLineSegment(sketch, "E153.left", {"start": v(36.9, 62.4) * mm, "end": v(36.9, 56.02) * mm});
            skLineSegment(sketch, "E154.bottom", {"start": v(21.64, 62.4) * mm, "end": v(35.63, 62.4) * mm});
            skLineSegment(sketch, "E154.top", {"start": v(21.64, 56.02) * mm, "end": v(35.63, 56.02) * mm});
            skLineSegment(sketch, "E153.top", {"start": v(36.9, 56.02) * mm, "end": v(50.9, 56.02) * mm});
            skLineSegment(sketch, "E155.bottom", {"start": v(67.43, 62.4) * mm, "end": v(81.43, 62.4) * mm});
            skLineSegment(sketch, "E156.left", {"start": v(52.17, 62.4) * mm, "end": v(52.17, 56.02) * mm});
            skLineSegment(sketch, "E156.right", {"start": v(66.16, 62.4) * mm, "end": v(66.16, 56.02) * mm});
            skLineSegment(sketch, "E155.right", {"start": v(81.43, 62.4) * mm, "end": v(81.43, 56.02) * mm});
            skLineSegment(sketch, "E155.left", {"start": v(67.43, 62.4) * mm, "end": v(67.43, 56.02) * mm});
            skLineSegment(sketch, "E156.bottom", {"start": v(52.17, 62.4) * mm, "end": v(66.16, 62.4) * mm});
            skLineSegment(sketch, "E156.top", {"start": v(52.17, 56.02) * mm, "end": v(66.16, 56.02) * mm});
            skLineSegment(sketch, "E155.top", {"start": v(67.43, 56.02) * mm, "end": v(81.43, 56.02) * mm});
            skLineSegment(sketch, "E157.bottom", {"start": v(97.96, 62.4) * mm, "end": v(109.42, 62.4) * mm});
            skLineSegment(sketch, "E158.left", {"start": v(82.7, 62.4) * mm, "end": v(82.7, 56.02) * mm});
            skLineSegment(sketch, "E158.right", {"start": v(96.7, 62.4) * mm, "end": v(96.7, 56.02) * mm});
            skLineSegment(sketch, "E157.right", {"start": v(111.96, 59.86) * mm, "end": v(111.96, 56.02) * mm});
            skLineSegment(sketch, "E157.left", {"start": v(97.96, 62.4) * mm, "end": v(97.96, 56.02) * mm});
            skLineSegment(sketch, "E158.bottom", {"start": v(82.7, 62.4) * mm, "end": v(96.7, 62.4) * mm});
            skLineSegment(sketch, "E158.top", {"start": v(82.7, 56.02) * mm, "end": v(96.7, 56.02) * mm});
            skLineSegment(sketch, "E157.top", {"start": v(97.96, 56.02) * mm, "end": v(111.96, 56.02) * mm});
            skPoint(sketch, "E159.visualSharp", {"position": v(111.96, 62.4) * mm});
            skArc(sketch, "E159.filletArc", {"start": v(111.96, 59.86) * mm, "mid": v(111.22, 61.65) * mm, "end": v(109.42, 62.4) * mm});
            skSolve(sketch);
        }
        {
            var Q0;
            Q0 = qSketchRegion(id + "F18", true);
            extrude(context, id + "F19", {"entities" : qUnion([Q0]), "depth" : 1.27 * mm});
        }
        {
            var Q0;
            Q0=makeQuery(id+"F3.imprint","IMPRINT",FACE,{"disambiguationData":[TD([[makeQuery(id+"F3.imprint","IMPRINT",EDGE,{"derivedFrom":sQuery(id+"F3.wireOp",EDGE,"E5.bottom")}),-1.0]])]});
            var sketch = newSketch(context, id + "F20", { "sketchPlane" : qUnion([Q0])});
            skLineSegment(sketch, "E160.bottom", {"start": v(-136.47, 78.45) * mm, "end": v(-109.77, 78.45) * mm});
            skLineSegment(sketch, "E160.top", {"start": v(-136.47, 70.57) * mm, "end": v(-109.77, 70.57) * mm});
            skLineSegment(sketch, "E160.left", {"start": v(-136.47, 78.45) * mm, "end": v(-136.47, 70.57) * mm});
            skLineSegment(sketch, "E160.right", {"start": v(-109.77, 78.45) * mm, "end": v(-109.77, 70.57) * mm});
            skSolve(sketch);
        }
        {
            var Q0;
            Q0 = qSketchRegion(id + "F20", true);
            extrude(context, id + "F21", {"entities" : qUnion([Q0]), "operationType" : NewBodyOperationType.REMOVE, "oppositeDirection" : true, "depth" : 0.13 * mm});
        }
        {
            var Q0;
            Q0=makeQuery(id+"F1.opExtrude","SWEPT_FACE",FACE,{"disambiguationData":[OSD([sQuery(id+"F0.wireOp",EDGE,"E0.right")])]});
            var sketch = newSketch(context, id + "F22", { "sketchPlane" : qUnion([Q0])});
            skLineSegment(sketch, "E161.bottom", {"start": v(-76.72, 9.96) * mm, "end": v(-58.55, 9.96) * mm});
            skLineSegment(sketch, "E161.top", {"start": v(-76.72, 5.08) * mm, "end": v(-58.55, 5.08) * mm});
            skLineSegment(sketch, "E161.left", {"start": v(-76.72, 9.96) * mm, "end": v(-76.72, 5.08) * mm});
            skLineSegment(sketch, "E161.right", {"start": v(-58.55, 9.96) * mm, "end": v(-58.55, 5.08) * mm});
            skLineSegment(sketch, "E162.bottom", {"start": v(-53.76, 9.97) * mm, "end": v(-33.82, 9.97) * mm});
            skLineSegment(sketch, "E162.top", {"start": v(-53.76, 5.08) * mm, "end": v(-33.82, 5.08) * mm});
            skLineSegment(sketch, "E162.left", {"start": v(-53.76, 9.97) * mm, "end": v(-53.76, 5.08) * mm});
            skLineSegment(sketch, "E162.right", {"start": v(-33.82, 9.97) * mm, "end": v(-33.82, 5.08) * mm});
            skSolve(sketch);
        }
        {
            var Q0;
            Q0=makeQuery(id+"F22.imprint","IMPRINT",FACE,{"disambiguationData":[TD([[makeQuery(id+"F22.imprint","IMPRINT",EDGE,{"derivedFrom":sQuery(id+"F22.wireOp",EDGE,"E161.bottom")}),-1.0]])]});
            var Q1;
            Q1=makeQuery(id+"F22.imprint","IMPRINT",FACE,{"disambiguationData":[TD([[makeQuery(id+"F22.imprint","IMPRINT",EDGE,{"derivedFrom":sQuery(id+"F22.wireOp",EDGE,"E162.bottom")}),-1.0]])]});
            extrude(context, id + "F23", {"entities" : qUnion([Q0, Q1]), "operationType" : NewBodyOperationType.REMOVE, "oppositeDirection" : true, "depth" : 12.7 * mm});
        }
    });
